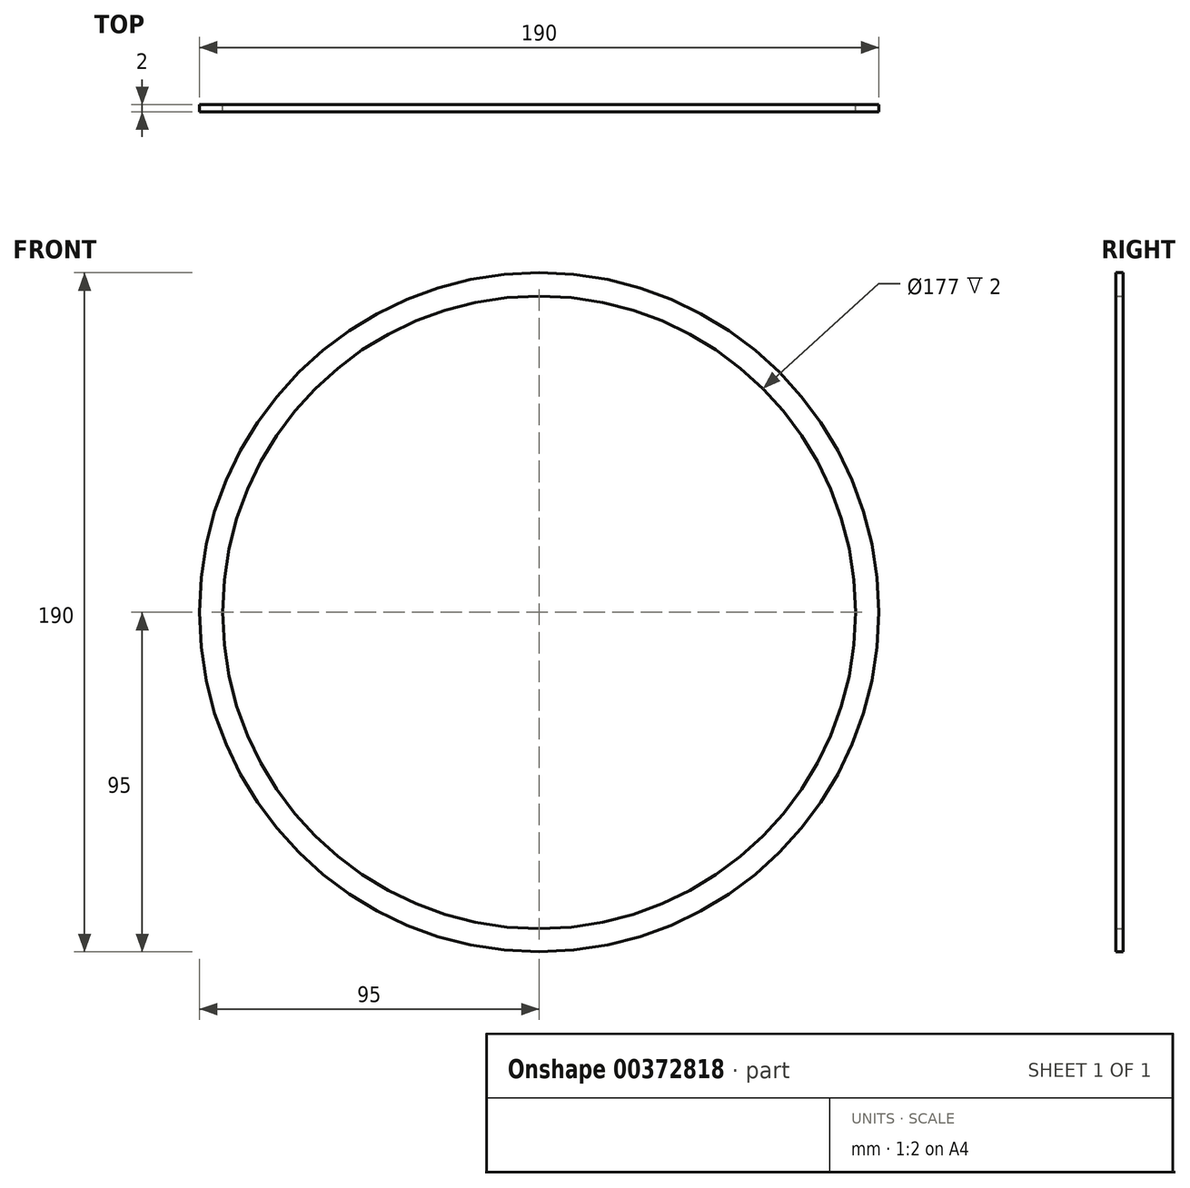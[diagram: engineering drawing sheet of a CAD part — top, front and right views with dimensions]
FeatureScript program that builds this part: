
annotation { "Feature Type Name" : "Feature", "Feature Type Description" : "" }
export const myFeature = defineFeature(function(context is Context, id is Id, definition is map)
    precondition{}
    {
        {
            var Q0;
            Q0=qCreatedBy(makeId("Front.planeOp"),FACE);
            var sketch = newSketch(context, id + "F0", { "sketchPlane" : qUnion([Q0])});
            skCircle(sketch, "E0", {"center": v(0, 0) * mm, "radius": 95 * mm});
            skCircle(sketch, "E1", {"center": v(0, 0) * mm, "radius": 87.5 * mm});
            skCircle(sketch, "E2", {"center": v(0, 0) * mm, "radius": 88.5 * mm});
            skSolve(sketch);
        }
        {
            var Q0;
            Q0=makeQuery(id+"F0.imprint","IMPRINT",FACE,{"disambiguationData":[TD([[makeQuery(id+"F0.imprint","IMPRINT",EDGE,{"derivedFrom":sQuery(id+"F0.wireOp",EDGE,"E0")}),1.0]])]});
            extrude(context, id + "F1", {"entities" : qUnion([Q0]), "depth" : 2 * mm});
        }
        {
            var Q0;
            Q0=sQuery(id+"F0.wireOp",EDGE,"E1");
            extrude(context, id + "F2", {"bodyType" : ToolBodyType.SURFACE, "surfaceEntities" : qUnion([Q0]), "depth" : 20 * mm});
        }
    });
